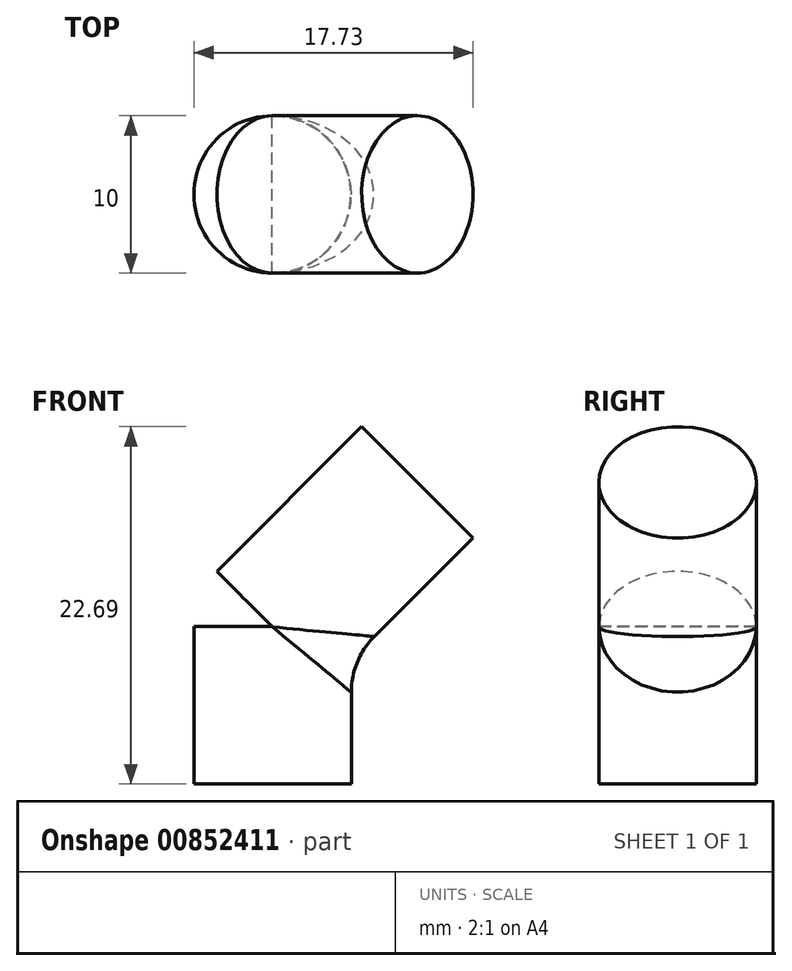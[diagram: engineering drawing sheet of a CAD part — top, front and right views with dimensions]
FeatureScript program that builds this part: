
annotation { "Feature Type Name" : "Feature", "Feature Type Description" : "" }
export const myFeature = defineFeature(function(context is Context, id is Id, definition is map)
    precondition{}
    {
        {
            var Q0;
            Q0=qCreatedBy(makeId("Top.planeOp"),FACE);
            cPlane(context, id + "F0", {"entities" : qUnion([Q0]), "cplaneType" : CPlaneType.OFFSET, "offset" : 9.96 * mm, "width" : 150 * mm, "height" : 150 * mm});
        }
        {
            var Q0;
            Q0=qCreatedBy(id+"F0.planeOp",FACE);
            var sketch = newSketch(context, id + "F1", { "sketchPlane" : qUnion([Q0])});
            skCircle(sketch, "E0", {"center": v(0, 0) * mm, "radius": 5 * mm});
            skSolve(sketch);
        }
        {
            var Q0;
            Q0 = qSketchRegion(id + "F1", true);
            extrude(context, id + "F2", {"entities" : qUnion([Q0]), "depth" : 13 * mm, "offsetDistance" : 25 * mm});
        }
        {
            var Q0;
            Q0=qCreatedBy(id+"F0.planeOp",FACE);
            var sketch = newSketch(context, id + "F3", { "sketchPlane" : qUnion([Q0])});
            skLineSegment(sketch, "E1", {"start": v(0, 0) * mm, "end": v(0, -34.9) * mm});
            skSolve(sketch);
        }
        {
            var Q0;
            Q0=makeQuery(id+"F2.opExtrude","SWEPT_BODY",BODY,{"disambiguationData":[OSD([sQuery(id+"F1.wireOp",EDGE,"E0")])]});
            var Q1;
            Q1=sQuery(id+"F3.wireOp",EDGE,"E1");
            transform(context, id + "F4", {"entities" : qUnion([Q0]), "transformType" : TransformType.ROTATION, "transformAxis" : qUnion([Q1]), "angle" : 45 * degree, "oppositeDirection" : true, "makeCopy" : false});
        }
        {
            var Q0;
            Q0=qCreatedBy(makeId("Top.planeOp"),FACE);
            var sketch = newSketch(context, id + "F5", { "sketchPlane" : qUnion([Q0])});
            skCircle(sketch, "E2", {"center": v(0, 0) * mm, "radius": 5 * mm});
            skSolve(sketch);
        }
        {
            var Q0;
            Q0 = qSketchRegion(id + "F5", true);
            extrude(context, id + "F6", {"entities" : qUnion([Q0]), "depth" : 10 * mm, "offsetDistance" : 25 * mm});
        }
        {
            var Q0;
            Q0=makeQuery(id+"F6.opExtrude","SWEPT_BODY",BODY,{"disambiguationData":[OSD([sQuery(id+"F5.wireOp",EDGE,"E2")])]});
            var Q1;
            Q1=makeQuery(id+"F2.opExtrude","SWEPT_BODY",BODY,{"disambiguationData":[OSD([sQuery(id+"F1.wireOp",EDGE,"E0")])]});
            booleanBodies(context, id + "F7", {"operationType" : BooleanOperationType.UNION, "tools" : qUnion([Q0, Q1])});
        }
        {
            var Q0;
            Q0=makeQuery(id+"F7.opBoolean","INTERSECT",EDGE,{"disambiguationData":[OD(0.0)],"derivedFrom":[makeQuery(id+"F6.opExtrude","SWEPT_FACE",FACE,{"disambiguationData":[OSD([sQuery(id+"F5.wireOp",EDGE,"E2")])]}),makeQuery(id+"F2.opExtrude","SWEPT_FACE",FACE,{"disambiguationData":[OSD([sQuery(id+"F1.wireOp",EDGE,"E0")])]})]});
            fillet(context, id + "F8", {"entities" : qUnion([Q0]), "radius" : 5 * mm, "tangentPropagation" : true, "allowEdgeOverflow" : false});
        }
    });
